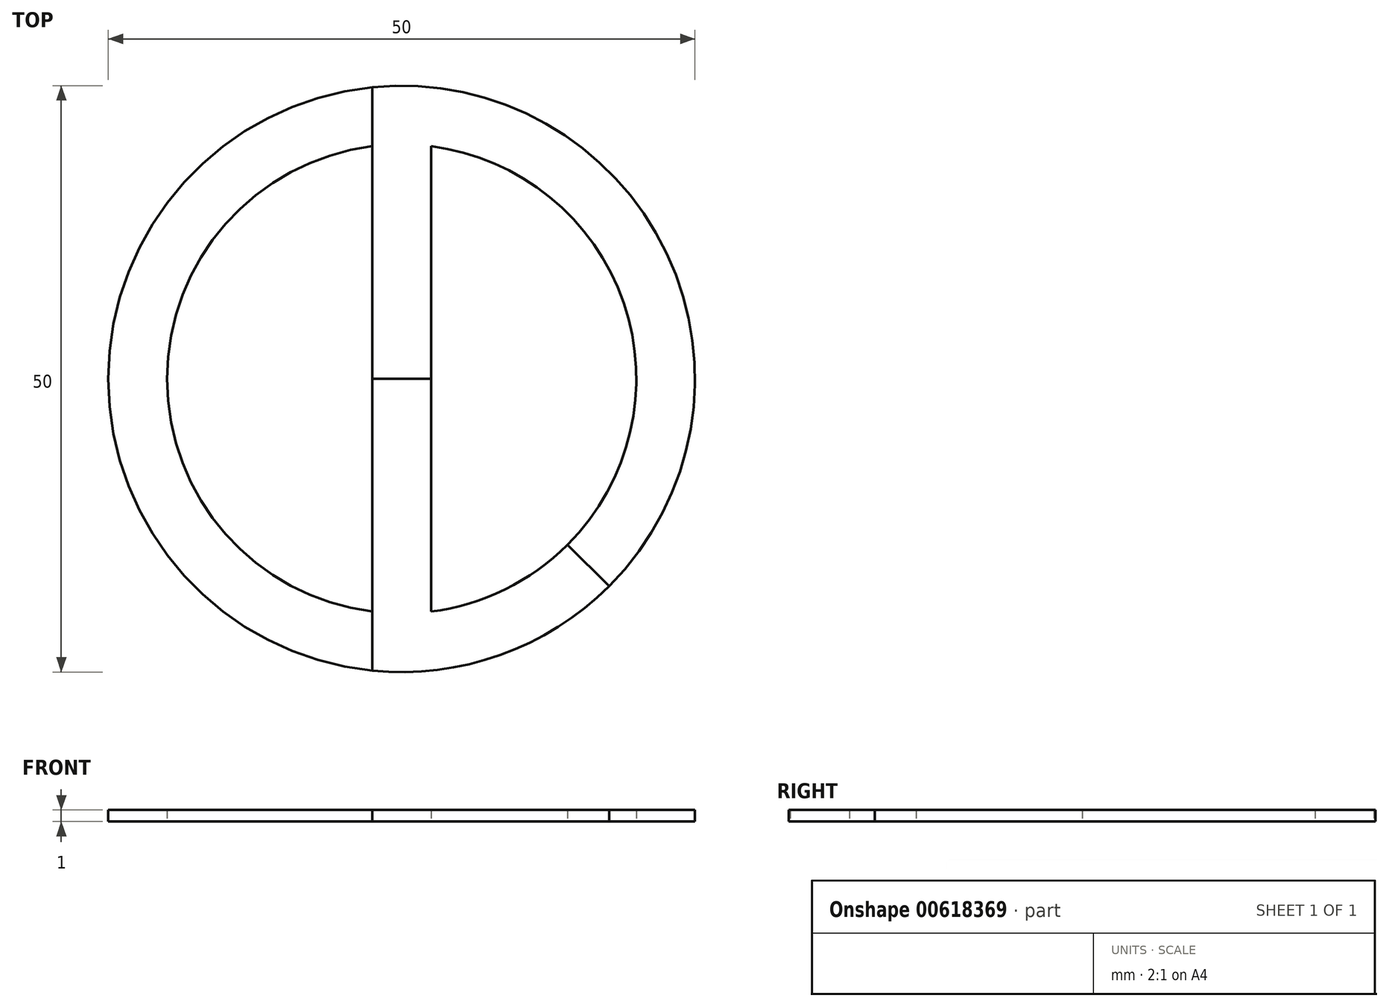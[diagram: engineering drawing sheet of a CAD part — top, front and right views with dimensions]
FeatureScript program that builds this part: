
annotation { "Feature Type Name" : "Feature", "Feature Type Description" : "" }
export const myFeature = defineFeature(function(context is Context, id is Id, definition is map)
    precondition{}
    {
        {
            var Q0;
            Q0=qCreatedBy(makeId("Top.planeOp"),FACE);
            var sketch = newSketch(context, id + "F0", { "sketchPlane" : qUnion([Q0])});
            skCircle(sketch, "E0", {"center": v(0, 0) * mm, "radius": 25 * mm});
            skArc(sketch, "E1", {"start": v(-2.5, 19.84) * mm, "mid": v(-20, 0) * mm, "end": v(-2.5, -19.84) * mm});
            skLineSegment(sketch, "E2", {"start": v(2.5, 0) * mm, "end": v(2.5, 19.84) * mm});
            skLineSegment(sketch, "E3", {"start": v(-2.5, 0) * mm, "end": v(-2.5, 19.84) * mm});
            skLineSegment(sketch, "E4", {"start": v(-2.5, 0) * mm, "end": v(-2.5, -19.84) * mm});
            skLineSegment(sketch, "E5", {"start": v(2.5, 0) * mm, "end": v(2.5, -19.84) * mm});
            skLineSegment(sketch, "E6", {"start": v(-2.5, 24.87) * mm, "end": v(-2.5, -24.87) * mm});
            skArc(sketch, "E7.trimOffspring", {"start": v(2.5, -19.84) * mm, "mid": v(20, 0) * mm, "end": v(2.5, 19.84) * mm});
            skLineSegment(sketch, "E8", {"start": v(14.14, -14.14) * mm, "end": v(17.68, -17.68) * mm});
            skLineSegment(sketch, "E9", {"start": v(-2.5, 0) * mm, "end": v(2.5, 0) * mm});
            skSolve(sketch);
        }
        {
            var Q0;
            {var subQ4=sQuery(id+"F0.wireOp",EDGE,"E1");Q0=makeQuery(id+"F0.imprint","IMPRINT",FACE,{"disambiguationData":[TD([[makeQuery(id+"F0.imprint","IMPRINT",EDGE,{"derivedFrom":subQ4}),-1.0]])]});}
            extrude(context, id + "F1", {"entities" : qUnion([Q0]), "depth" : 1 * mm, "offsetDistance" : 25 * mm});
        }
        {
            var Q0;
            {var subQ4=sQuery(id+"F0.wireOp",EDGE,"E2");Q0=makeQuery(id+"F0.imprint","IMPRINT",FACE,{"disambiguationData":[TD([[makeQuery(id+"F0.imprint","IMPRINT",EDGE,{"derivedFrom":subQ4}),1.0]])]});}
            extrude(context, id + "F2", {"entities" : qUnion([Q0]), "depth" : 1 * mm, "offsetDistance" : 25 * mm});
        }
        {
            var Q0;
            {var subQ5=sQuery(id+"F0.wireOp",EDGE,"E5");Q0=makeQuery(id+"F0.imprint","IMPRINT",FACE,{"disambiguationData":[TD([[makeQuery(id+"F0.imprint","IMPRINT",EDGE,{"derivedFrom":subQ5}),-1.0]])]});}
            extrude(context, id + "F3", {"entities" : qUnion([Q0]), "depth" : 1 * mm, "offsetDistance" : 25 * mm});
        }
    });
